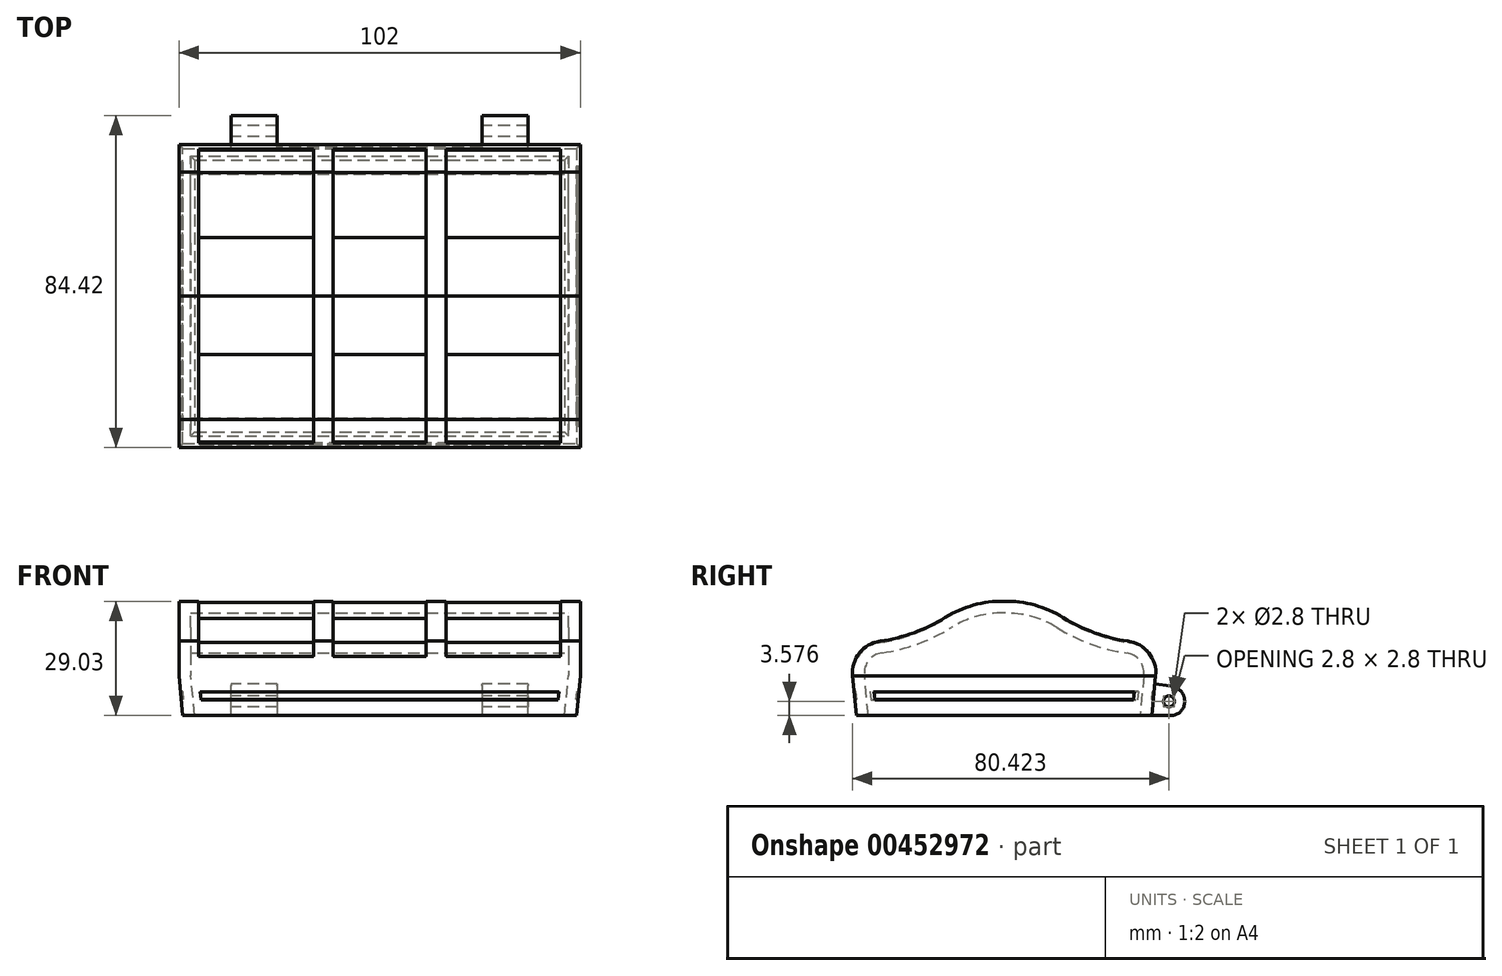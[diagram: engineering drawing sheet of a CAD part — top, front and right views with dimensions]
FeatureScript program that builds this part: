
annotation { "Feature Type Name" : "Feature", "Feature Type Description" : "" }
export const myFeature = defineFeature(function(context is Context, id is Id, definition is map)
    precondition{}
    {
        {
            var Q0;
            Q0=qCreatedBy(makeId("Right.planeOp"),FACE);
            cPlane(context, id + "F0", {"entities" : qUnion([Q0]), "cplaneType" : CPlaneType.OFFSET, "offset" : 51 * mm, "width" : 150 * mm, "height" : 150 * mm});
        }
        {
            var Q0;
            Q0=qCreatedBy(id+"F0.planeOp",FACE);
            var sketch = newSketch(context, id + "F1", { "sketchPlane" : qUnion([Q0])});
            skLineSegment(sketch, "E0", {"start": v(37.5, 0) * mm, "end": v(-37.5, 0) * mm});
            skArc(sketch, "E1", {"start": v(-31.43, 18.88) * mm, "mid": v(-22.9, 21.03) * mm, "end": v(-15, 24.87) * mm});
            skArc(sketch, "E2", {"start": v(0, 29.03) * mm, "mid": v(-7.8, 28.02) * mm, "end": v(-15, 24.87) * mm});
            skArc(sketch, "E3", {"start": v(-31.43, 18.88) * mm, "mid": v(-36.77, 15.87) * mm, "end": v(-38.5, 10) * mm});
            skArc(sketch, "E4.MirrorCS", {"start": v(31.43, 18.88) * mm, "mid": v(22.9, 21.03) * mm, "end": v(15, 24.87) * mm});
            skArc(sketch, "E5.MirrorCS", {"start": v(31.43, 18.88) * mm, "mid": v(36.77, 15.87) * mm, "end": v(38.5, 10) * mm});
            skArc(sketch, "E6.MirrorCS", {"start": v(0, 29.03) * mm, "mid": v(7.8, 28.02) * mm, "end": v(15, 24.87) * mm});
            skLineSegment(sketch, "E7", {"start": v(38.5, 10) * mm, "end": v(37.5, 0) * mm});
            skLineSegment(sketch, "E8", {"start": v(-37.5, 0) * mm, "end": v(-38.5, 10) * mm});
            skSolve(sketch);
        }
        {
            var Q0;
            Q0 = qSketchRegion(id + "F1", true);
            extrude(context, id + "F2", {"entities" : qUnion([Q0]), "oppositeDirection" : true, "depth" : 102 * mm, "offsetDistance" : 25 * mm});
        }
        {
            var Q0;
            Q0=makeQuery(id+"F2.opExtrude","CAP_EDGE",EDGE,{"disambiguationData":[OSD([sQuery(id+"F1.wireOp",EDGE,"E0")])],"isStart":true});
            var Q1;
            Q1=makeQuery(id+"F2.opExtrude","CAP_EDGE",EDGE,{"disambiguationData":[OSD([sQuery(id+"F1.wireOp",EDGE,"E0")])],"isStart":false});
            chamfer(context, id + "F3", {"entities" : qUnion([Q0, Q1]), "chamferType" : ChamferType.TWO_OFFSETS, "width1" : 1 * mm, "oppositeDirection" : false, "width2" : 10 * mm, "tangentPropagation" : true});
        }
        {
            var Q0;
            Q0=makeQuery(id+"F7.boolean.opBoolean","MERGE",FACE,{"derivedFrom":[makeQuery(id+"F2.opExtrude","SWEPT_FACE",FACE,{"disambiguationData":[OSD([sQuery(id+"F1.wireOp",EDGE,"E0")])]}),makeQuery(id+"F7.opExtrude","SWEPT_FACE",FACE,{"disambiguationData":[OSD([sQuery(id+"F6.wireOp",EDGE,"E12"),sQuery(id+"F6.wireOp",EDGE,"E16")])]})]});
            shell(context, id + "F4", {"entities" : qUnion([Q0]), "thickness" : 3 * mm});
        }
        {
            var Q0;
            Q0=qCreatedBy(makeId("Right.planeOp"),FACE);
            cPlane(context, id + "F5", {"entities" : qUnion([Q0]), "cplaneType" : CPlaneType.OFFSET, "offset" : 37.75 * mm, "oppositeDirection" : true, "width" : 150 * mm, "height" : 150 * mm});
        }
        {
            var Q0;
            Q0=qCreatedBy(id+"F5.planeOp",FACE);
            var sketch = newSketch(context, id + "F6", { "sketchPlane" : qUnion([Q0])});
            skLineSegment(sketch, "E9.0", {"start": v(45.54, 0) * mm, "end": v(45.86, 3.17) * mm});
            skLineSegment(sketch, "E10.0", {"start": v(38.3, 7.96) * mm, "end": v(42.29, 7.56) * mm});
            skPoint(sketch, "E11.visualSharp", {"position": v(46.27, 7.15) * mm});
            skArc(sketch, "E11.filletArc", {"start": v(45.86, 3.17) * mm, "mid": v(44.98, 6.1) * mm, "end": v(42.29, 7.56) * mm});
            skLineSegment(sketch, "E12", {"start": v(37.5, 0) * mm, "end": v(45.54, 0) * mm});
            skCircle(sketch, "E13", {"center": v(41.88, 3.58) * mm, "radius": 1.4 * mm});
            skLineSegment(sketch, "E14", {"start": v(38.14, 7.96) * mm, "end": v(37.34, 0) * mm});
            skLineSegment(sketch, "E15", {"start": v(38.14, 7.96) * mm, "end": v(38.3, 7.96) * mm});
            skLineSegment(sketch, "E16", {"start": v(37.34, 0) * mm, "end": v(37.5, 0) * mm});
            skSolve(sketch);
        }
        {
            var Q0;
            Q0 = qSketchRegion(id + "F6", true);
            extrude(context, id + "F7", {"entities" : qUnion([Q0]), "operationType" : NewBodyOperationType.ADD, "depth" : 75.5 * mm, "offsetDistance" : 25 * mm});
        }
        {
            var Q0;
            Q0=makeQuery(id+"F7.opExtrude","SWEPT_EDGE",EDGE,{"disambiguationData":[OSD([sQuery(id+"F6.wireOp",EDGE,"E9.0"),sQuery(id+"F6.wireOp",EDGE,"E12")])]});
            fillet(context, id + "F8", {"entities" : qUnion([Q0]), "radius" : 3.5 * mm, "tangentPropagation" : true, "allowEdgeOverflow" : false});
        }
        {
            var Q0;
            Q0=makeQuery(id+"F2.opExtrude","SWEPT_FACE",FACE,{"disambiguationData":[OSD([sQuery(id+"F1.wireOp",EDGE,"E7")])]});
            var sketch = newSketch(context, id + "F9", { "sketchPlane" : qUnion([Q0])});
            skLineSegment(sketch, "E17.bottom", {"start": v(-26, 12.12) * mm, "end": v(26, 12.12) * mm});
            skLineSegment(sketch, "E17.top", {"start": v(-26, 3.13) * mm, "end": v(26, 3.13) * mm});
            skLineSegment(sketch, "E17.left", {"start": v(-26, 12.12) * mm, "end": v(-26, 3.13) * mm});
            skLineSegment(sketch, "E17.right", {"start": v(26, 12.12) * mm, "end": v(26, 3.13) * mm});
            skSolve(sketch);
        }
        {
            var Q0;
            Q0 = qSketchRegion(id + "F9", true);
            extrude(context, id + "F10", {"entities" : qUnion([Q0]), "operationType" : NewBodyOperationType.REMOVE, "depth" : 8.5 * mm, "offsetDistance" : 25 * mm});
        }
        {
            var Q0;
            Q0=makeQuery(id+"F2.opExtrude","SWEPT_FACE",FACE,{"disambiguationData":[OSD([sQuery(id+"F1.wireOp",EDGE,"E8")])]});
            var sketch = newSketch(context, id + "F11", { "sketchPlane" : qUnion([Q0])});
            skLineSegment(sketch, "E18.0", {"start": v(-45.58, 9.78) * mm, "end": v(45.58, 9.78) * mm});
            skLineSegment(sketch, "E19.0", {"start": v(45.37, 7.73) * mm, "end": v(-45.37, 7.73) * mm});
            skLineSegment(sketch, "E20", {"start": v(-45.37, 7.73) * mm, "end": v(-45.58, 9.78) * mm});
            skLineSegment(sketch, "E21", {"start": v(45.58, 9.78) * mm, "end": v(45.37, 7.73) * mm});
            skSolve(sketch);
        }
        {
            var Q0;
            Q0 = qSketchRegion(id + "F11", true);
            extrude(context, id + "F12", {"entities" : qUnion([Q0]), "operationType" : NewBodyOperationType.REMOVE, "oppositeDirection" : true, "depth" : .5 * mm, "offsetDistance" : 25 * mm});
        }
        {
            var Q0;
            {var subQ0=sQuery(id+"F1.wireOp",EDGE,"E0");Q0=makeQuery(id+"F3.opChamfer","BLEND_FACE",FACE,{"disambiguationData":[OSD([subQ0]),TDD([makeQuery(id+"F2.opExtrude","CAP_EDGE",EDGE,{"disambiguationData":[OSD([subQ0])],"isStart":true})])]});}
            var sketch = newSketch(context, id + "F13", { "sketchPlane" : qUnion([Q0])});
            skLineSegment(sketch, "E22.0", {"start": v(-33.08, 11.03) * mm, "end": v(33.08, 11.03) * mm});
            skLineSegment(sketch, "E23.0", {"start": v(32.87, 8.98) * mm, "end": v(-32.87, 8.98) * mm});
            skLineSegment(sketch, "E24", {"start": v(-32.87, 8.98) * mm, "end": v(-33.08, 11.03) * mm});
            skLineSegment(sketch, "E25", {"start": v(33.08, 11.03) * mm, "end": v(32.87, 8.98) * mm});
            skSolve(sketch);
        }
        {
            var Q0;
            Q0 = qSketchRegion(id + "F13", true);
            extrude(context, id + "F14", {"entities" : qUnion([Q0]), "operationType" : NewBodyOperationType.REMOVE, "oppositeDirection" : true, "depth" : .5 * mm, "offsetDistance" : 25 * mm});
        }
        {
            var Q0;
            Q0=makeQuery(id+"F10.boolean.opBoolean","MERGE",FACE,{"derivedFrom":[makeQuery(id+"F2.opExtrude","SWEPT_FACE",FACE,{"disambiguationData":[OSD([sQuery(id+"F1.wireOp",EDGE,"E7")])]})],"fromTools":[makeQuery(id+"F10.opExtrude","CAP_FACE",FACE,{"disambiguationData":[OSD([sQuery(id+"F9.wireOp",EDGE,"E17.bottom"),sQuery(id+"F9.wireOp",EDGE,"E17.top"),sQuery(id+"F9.wireOp",EDGE,"E17.left"),sQuery(id+"F9.wireOp",EDGE,"E17.right")])],"isStart":true})]});
            var sketch = newSketch(context, id + "F15", { "sketchPlane" : qUnion([Q0])});
            skLineSegment(sketch, "E26.0", {"start": v(-26, 7.73) * mm, "end": v(26, 7.73) * mm});
            skLineSegment(sketch, "E27.0", {"start": v(-26, 9.73) * mm, "end": v(26, 9.73) * mm});
            skLineSegment(sketch, "E28", {"start": v(-26, 7.73) * mm, "end": v(-26, 9.73) * mm});
            skLineSegment(sketch, "E29", {"start": v(26, 7.73) * mm, "end": v(26, 9.73) * mm});
            skSolve(sketch);
        }
        {
            var Q0;
            Q0 = qSketchRegion(id + "F15", true);
            extrude(context, id + "F16", {"entities" : qUnion([Q0]), "operationType" : NewBodyOperationType.REMOVE, "oppositeDirection" : true, "depth" : .5 * mm, "offsetDistance" : 25 * mm});
        }
        {
            var Q0;
            {var subQ0=sQuery(id+"F1.wireOp",EDGE,"E0");Q0=makeQuery(id+"F3.opChamfer","BLEND_FACE",FACE,{"disambiguationData":[OSD([subQ0]),TDD([makeQuery(id+"F2.opExtrude","CAP_EDGE",EDGE,{"disambiguationData":[OSD([subQ0])],"isStart":false})])]});}
            var sketch = newSketch(context, id + "F17", { "sketchPlane" : qUnion([Q0])});
            skLineSegment(sketch, "E30.0", {"start": v(-34.08, 11.03) * mm, "end": v(34.08, 11.03) * mm});
            skLineSegment(sketch, "E31.0", {"start": v(33.88, 8.98) * mm, "end": v(-33.88, 8.98) * mm});
            skLineSegment(sketch, "E32", {"start": v(-34.08, 11.03) * mm, "end": v(-33.88, 8.98) * mm});
            skLineSegment(sketch, "E33", {"start": v(34.08, 11.03) * mm, "end": v(33.88, 8.98) * mm});
            skSolve(sketch);
        }
        {
            var Q0;
            Q0 = qSketchRegion(id + "F17", true);
            extrude(context, id + "F18", {"entities" : qUnion([Q0]), "operationType" : NewBodyOperationType.REMOVE, "oppositeDirection" : true, "depth" : .5 * mm, "offsetDistance" : 25 * mm});
        }
        {
            var Q0;
            Q0=qCreatedBy(makeId("Right.planeOp"),FACE);
            cPlane(context, id + "F19", {"entities" : qUnion([Q0]), "cplaneType" : CPlaneType.OFFSET, "offset" : 11.82 * mm, "width" : 150 * mm, "height" : 150 * mm});
        }
        {
            var Q0;
            Q0=qCreatedBy(id+"F19.planeOp",FACE);
            var sketch = newSketch(context, id + "F20", { "sketchPlane" : qUnion([Q0])});
            skArc(sketch, "E34", {"start": v(-31.43, 18.88) * mm, "mid": v(-22.9, 21.03) * mm, "end": v(-15, 24.87) * mm});
            skArc(sketch, "E35", {"start": v(0, 29.03) * mm, "mid": v(-7.8, 28.02) * mm, "end": v(-15, 24.87) * mm});
            skArc(sketch, "E36", {"start": v(-31.43, 18.88) * mm, "mid": v(-34.85, 17.62) * mm, "end": v(-37.38, 15) * mm});
            skArc(sketch, "E37", {"start": v(-31.39, 18.53) * mm, "mid": v(-34.7, 17.37) * mm, "end": v(-37.13, 14.85) * mm});
            skArc(sketch, "E38", {"start": v(-31.39, 18.53) * mm, "mid": v(-22.82, 20.77) * mm, "end": v(-14.84, 24.6) * mm});
            skArc(sketch, "E39", {"start": v(0, 28.77) * mm, "mid": v(-7.73, 27.8) * mm, "end": v(-14.84, 24.6) * mm});
            skArc(sketch, "E40.MirrorCS", {"start": v(31.43, 18.88) * mm, "mid": v(34.85, 17.62) * mm, "end": v(37.38, 15) * mm});
            skArc(sketch, "E41.MirrorCS", {"start": v(0, 28.77) * mm, "mid": v(7.73, 27.8) * mm, "end": v(14.84, 24.6) * mm});
            skArc(sketch, "E42.MirrorCS", {"start": v(31.43, 18.88) * mm, "mid": v(22.9, 21.03) * mm, "end": v(15, 24.87) * mm});
            skArc(sketch, "E43.MirrorCS", {"start": v(31.39, 18.53) * mm, "mid": v(22.82, 20.77) * mm, "end": v(14.84, 24.6) * mm});
            skArc(sketch, "E44.MirrorCS", {"start": v(31.39, 18.53) * mm, "mid": v(34.7, 17.37) * mm, "end": v(37.13, 14.85) * mm});
            skArc(sketch, "E45.MirrorCS", {"start": v(0, 29.03) * mm, "mid": v(7.8, 28.02) * mm, "end": v(15, 24.87) * mm});
            skPoint(sketch, "E46.orphan", {"position": v(0, 28.77) * mm});
            skLineSegment(sketch, "E47", {"start": v(-37.38, 15) * mm, "end": v(-37.13, 14.85) * mm});
            skLineSegment(sketch, "E48", {"start": v(37.13, 14.85) * mm, "end": v(37.38, 15) * mm});
            skSolve(sketch);
        }
        {
            var Q0;
            Q0 = qSketchRegion(id + "F20", true);
            extrude(context, id + "F21", {"entities" : qUnion([Q0]), "operationType" : NewBodyOperationType.REMOVE, "oppositeDirection" : true, "depth" : 23.65 * mm, "offsetDistance" : 25 * mm});
        }
        {
            var Q0;
            Q0=qCreatedBy(id+"F19.planeOp",FACE);
            cPlane(context, id + "F22", {"entities" : qUnion([Q0]), "cplaneType" : CPlaneType.OFFSET, "offset" : 5 * mm, "width" : 150 * mm, "height" : 150 * mm});
        }
        {
            var Q0;
            Q0=qCreatedBy(id+"F22.planeOp",FACE);
            var sketch = newSketch(context, id + "F23", { "sketchPlane" : qUnion([Q0])});
            skArc(sketch, "E49", {"start": v(-31.43, 18.88) * mm, "mid": v(-22.9, 21.03) * mm, "end": v(-15, 24.87) * mm});
            skArc(sketch, "E50", {"start": v(0, 29.03) * mm, "mid": v(-7.8, 28.02) * mm, "end": v(-15, 24.87) * mm});
            skArc(sketch, "E51", {"start": v(-31.43, 18.88) * mm, "mid": v(-34.85, 17.62) * mm, "end": v(-37.38, 15) * mm});
            skArc(sketch, "E52", {"start": v(-31.39, 18.53) * mm, "mid": v(-34.7, 17.37) * mm, "end": v(-37.13, 14.85) * mm});
            skArc(sketch, "E53", {"start": v(-31.39, 18.53) * mm, "mid": v(-22.82, 20.77) * mm, "end": v(-14.84, 24.6) * mm});
            skArc(sketch, "E54", {"start": v(0, 28.77) * mm, "mid": v(-7.73, 27.8) * mm, "end": v(-14.84, 24.6) * mm});
            skArc(sketch, "E55.MirrorCS", {"start": v(31.43, 18.88) * mm, "mid": v(34.85, 17.62) * mm, "end": v(37.38, 15) * mm});
            skArc(sketch, "E56.MirrorCS", {"start": v(0, 28.77) * mm, "mid": v(7.73, 27.8) * mm, "end": v(14.84, 24.6) * mm});
            skArc(sketch, "E57.MirrorCS", {"start": v(31.43, 18.88) * mm, "mid": v(22.9, 21.03) * mm, "end": v(15, 24.87) * mm});
            skArc(sketch, "E58.MirrorCS", {"start": v(31.39, 18.53) * mm, "mid": v(22.82, 20.77) * mm, "end": v(14.84, 24.6) * mm});
            skArc(sketch, "E59.MirrorCS", {"start": v(31.39, 18.53) * mm, "mid": v(34.7, 17.37) * mm, "end": v(37.13, 14.85) * mm});
            skArc(sketch, "E60.MirrorCS", {"start": v(0, 29.03) * mm, "mid": v(7.8, 28.02) * mm, "end": v(15, 24.87) * mm});
            skPoint(sketch, "E61.orphan", {"position": v(0, 28.77) * mm});
            skLineSegment(sketch, "E62", {"start": v(-37.38, 15) * mm, "end": v(-37.13, 14.85) * mm});
            skLineSegment(sketch, "E63", {"start": v(37.13, 14.85) * mm, "end": v(37.38, 15) * mm});
            skSolve(sketch);
        }
        {
            var Q0;
            Q0 = qSketchRegion(id + "F23", true);
            extrude(context, id + "F24", {"entities" : qUnion([Q0]), "operationType" : NewBodyOperationType.REMOVE, "depth" : 29.15 * mm, "offsetDistance" : 25 * mm});
        }
        {
            var Q0;
            Q0=qCreatedBy(makeId("Right.planeOp"),FACE);
            cPlane(context, id + "F25", {"entities" : qUnion([Q0]), "cplaneType" : CPlaneType.OFFSET, "offset" : 16.82 * mm, "oppositeDirection" : true, "width" : 150 * mm, "height" : 150 * mm});
        }
        {
            var Q0;
            Q0=qCreatedBy(id+"F25.planeOp",FACE);
            var sketch = newSketch(context, id + "F26", { "sketchPlane" : qUnion([Q0])});
            skArc(sketch, "E64", {"start": v(-31.43, 18.88) * mm, "mid": v(-22.9, 21.03) * mm, "end": v(-15, 24.87) * mm});
            skArc(sketch, "E65", {"start": v(0, 29.03) * mm, "mid": v(-7.8, 28.02) * mm, "end": v(-15, 24.87) * mm});
            skArc(sketch, "E66", {"start": v(-31.43, 18.88) * mm, "mid": v(-34.85, 17.62) * mm, "end": v(-37.38, 15) * mm});
            skArc(sketch, "E67", {"start": v(-31.39, 18.53) * mm, "mid": v(-34.7, 17.37) * mm, "end": v(-37.13, 14.85) * mm});
            skArc(sketch, "E68", {"start": v(-31.39, 18.53) * mm, "mid": v(-22.82, 20.77) * mm, "end": v(-14.84, 24.6) * mm});
            skArc(sketch, "E69", {"start": v(0, 28.77) * mm, "mid": v(-7.73, 27.8) * mm, "end": v(-14.84, 24.6) * mm});
            skArc(sketch, "E70.MirrorCS", {"start": v(31.43, 18.88) * mm, "mid": v(34.85, 17.62) * mm, "end": v(37.38, 15) * mm});
            skArc(sketch, "E71.MirrorCS", {"start": v(0, 28.77) * mm, "mid": v(7.73, 27.8) * mm, "end": v(14.84, 24.6) * mm});
            skArc(sketch, "E72.MirrorCS", {"start": v(31.43, 18.88) * mm, "mid": v(22.9, 21.03) * mm, "end": v(15, 24.87) * mm});
            skArc(sketch, "E73.MirrorCS", {"start": v(31.39, 18.53) * mm, "mid": v(22.82, 20.77) * mm, "end": v(14.84, 24.6) * mm});
            skArc(sketch, "E74.MirrorCS", {"start": v(31.39, 18.53) * mm, "mid": v(34.7, 17.37) * mm, "end": v(37.13, 14.85) * mm});
            skArc(sketch, "E75.MirrorCS", {"start": v(0, 29.03) * mm, "mid": v(7.8, 28.02) * mm, "end": v(15, 24.87) * mm});
            skPoint(sketch, "E76.orphan", {"position": v(0, 28.77) * mm});
            skLineSegment(sketch, "E77", {"start": v(-37.38, 15) * mm, "end": v(-37.13, 14.85) * mm});
            skLineSegment(sketch, "E78", {"start": v(37.13, 14.85) * mm, "end": v(37.38, 15) * mm});
            skSolve(sketch);
        }
        {
            var Q0;
            Q0 = qSketchRegion(id + "F26", true);
            extrude(context, id + "F27", {"entities" : qUnion([Q0]), "operationType" : NewBodyOperationType.REMOVE, "oppositeDirection" : true, "depth" : 29.15 * mm, "offsetDistance" : 25 * mm});
        }
    });
